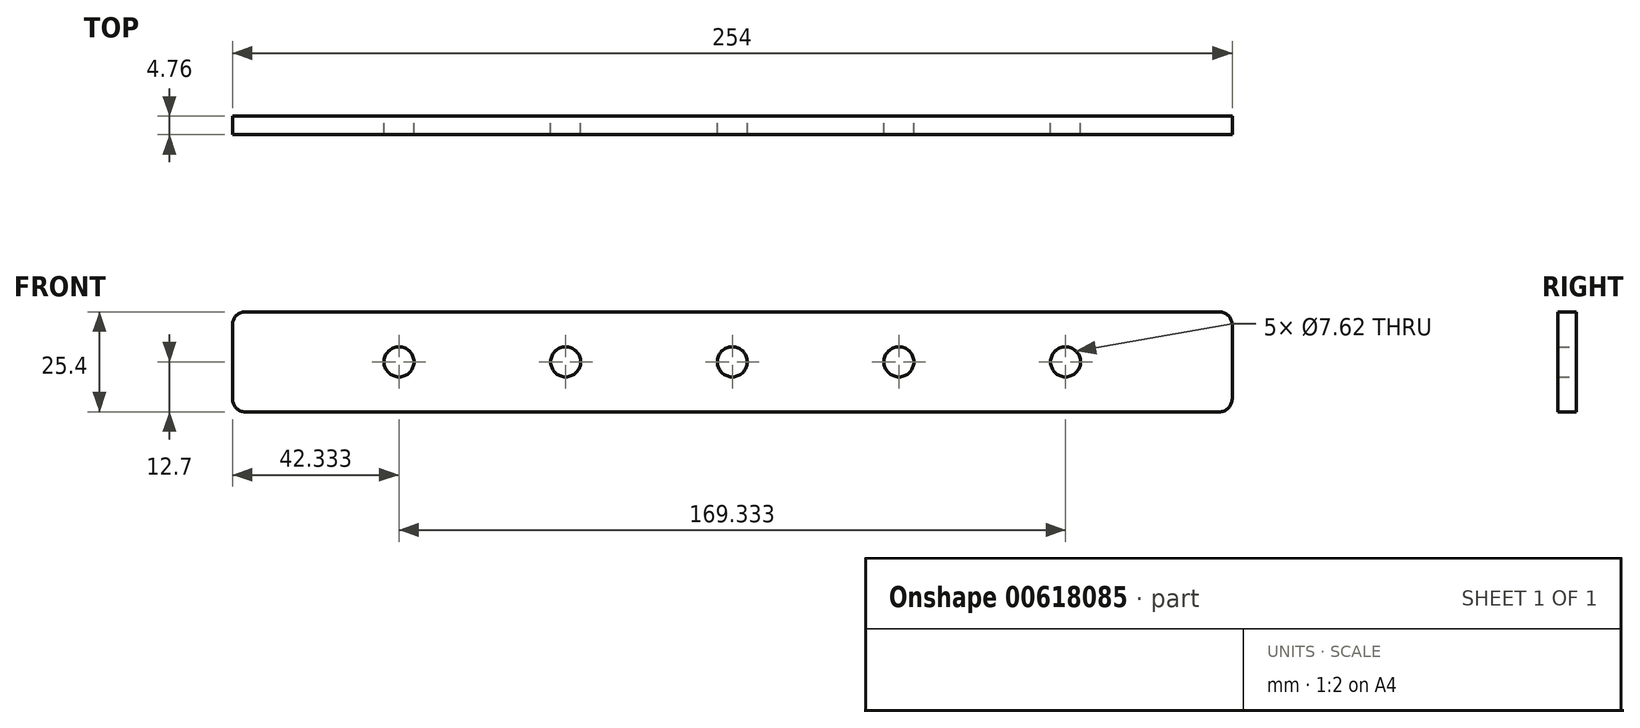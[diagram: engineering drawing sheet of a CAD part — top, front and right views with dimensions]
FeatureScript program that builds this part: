
annotation { "Feature Type Name" : "Feature", "Feature Type Description" : "" }
export const myFeature = defineFeature(function(context is Context, id is Id, definition is map)
    precondition{}
    {
        {
            var Q0;
            Q0=qCreatedBy(makeId("Front.planeOp"),FACE);
            var sketch = newSketch(context, id + "F0", { "sketchPlane" : qUnion([Q0])});
            skLineSegment(sketch, "E0.bottom", {"start": v(123.7, 12.7) * mm, "end": v(-123.7, 12.7) * mm});
            skLineSegment(sketch, "E0.top", {"start": v(123.7, -12.7) * mm, "end": v(-123.7, -12.7) * mm});
            skLineSegment(sketch, "E0.left", {"start": v(127, 9.4) * mm, "end": v(127, -9.4) * mm});
            skLineSegment(sketch, "E0.right", {"start": v(-127, 9.4) * mm, "end": v(-127, -9.4) * mm});
            skPoint(sketch, "E0.middle", {"position": v(0, 0) * mm});
            skPoint(sketch, "E1.visualSharp", {"position": v(-127, 12.7) * mm});
            skArc(sketch, "E1.filletArc", {"start": v(-123.7, 12.7) * mm, "mid": v(-126.03, 11.73) * mm, "end": v(-127, 9.4) * mm});
            skPoint(sketch, "E2.visualSharp", {"position": v(-127, -12.7) * mm});
            skArc(sketch, "E2.filletArc", {"start": v(-127, -9.4) * mm, "mid": v(-126.03, -11.73) * mm, "end": v(-123.7, -12.7) * mm});
            skPoint(sketch, "E3.visualSharp", {"position": v(127, -12.7) * mm});
            skArc(sketch, "E3.filletArc", {"start": v(123.7, -12.7) * mm, "mid": v(126.03, -11.73) * mm, "end": v(127, -9.4) * mm});
            skPoint(sketch, "E4.visualSharp", {"position": v(127, 12.7) * mm});
            skArc(sketch, "E4.filletArc", {"start": v(127, 9.4) * mm, "mid": v(126.03, 11.73) * mm, "end": v(123.7, 12.7) * mm});
            skLineSegment(sketch, "E5", {"start": v(-127, 0) * mm, "end": v(127, 0) * mm, "construction": true});
            skCircle(sketch, "E6", {"center": v(-84.67, 0) * mm, "radius": 3.81 * mm});
            skCircle(sketch, "E7.1.0.0", {"center": v(-42.33, 0) * mm, "radius": 3.81 * mm});
            skCircle(sketch, "E7.2.0.0", {"center": v(0, 0) * mm, "radius": 3.81 * mm});
            skCircle(sketch, "E7.3.0.0", {"center": v(42.33, 0) * mm, "radius": 3.81 * mm});
            skCircle(sketch, "E7.4.0.0", {"center": v(84.67, 0) * mm, "radius": 3.81 * mm});
            skLineSegment(sketch, "E7.direction1", {"start": v(-84.67, 0) * mm, "end": v(-42.33, 0) * mm, "construction": true});
            skSolve(sketch);
        }
        {
            var Q0;
            Q0 = qSketchRegion(id + "F0", true);
            extrude(context, id + "F1", {"entities" : qUnion([Q0]), "depth" : 4.76 * mm, "offsetDistance" : 25.4 * mm});
        }
    });
